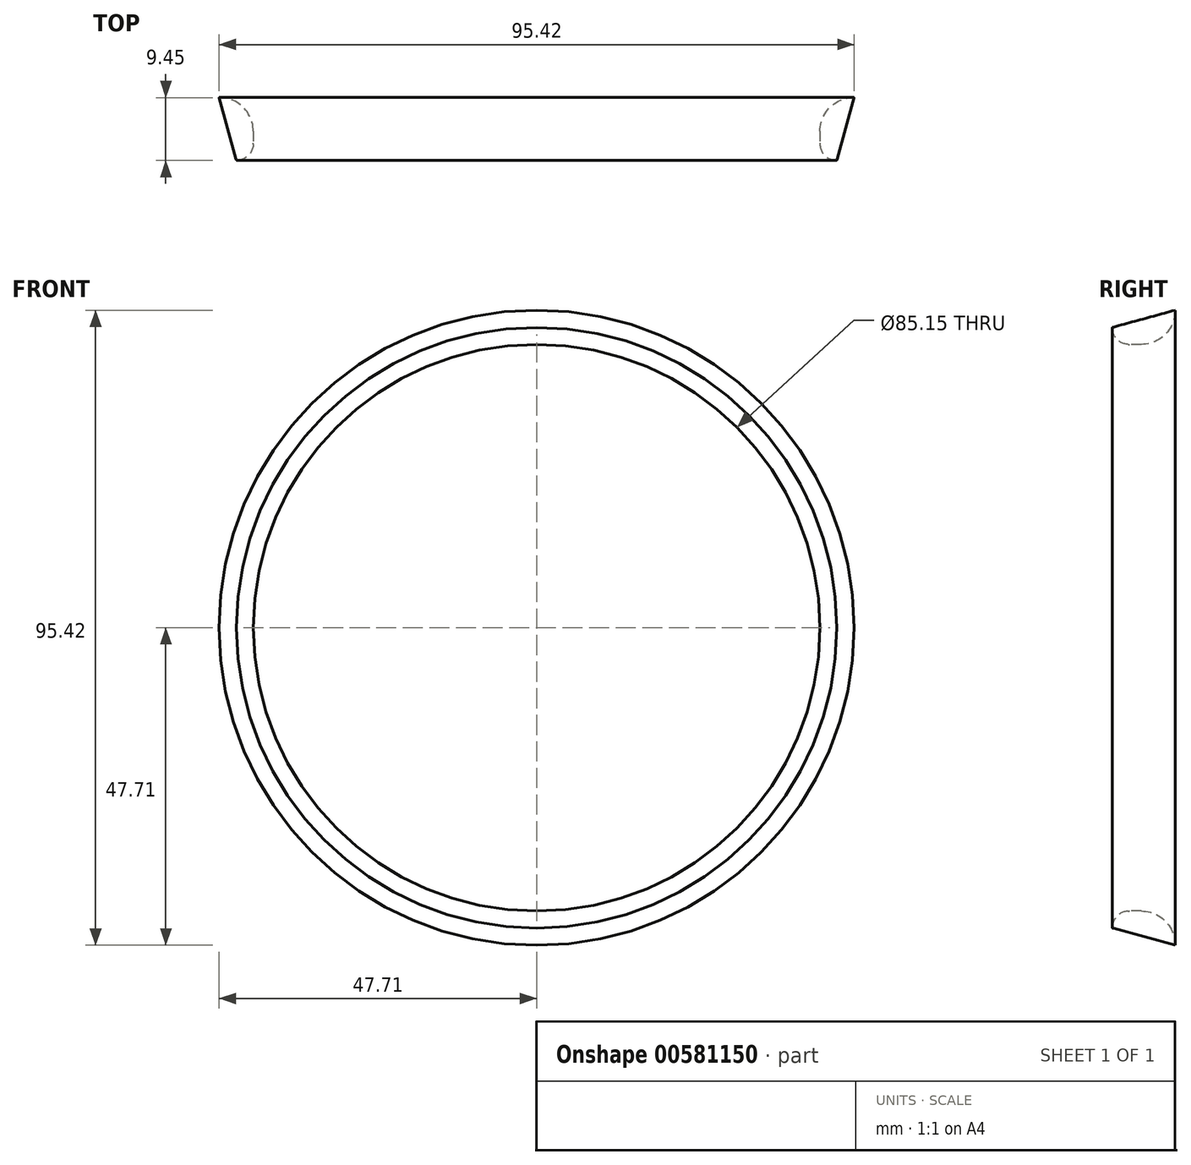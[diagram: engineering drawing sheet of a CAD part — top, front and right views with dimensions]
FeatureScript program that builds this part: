
annotation { "Feature Type Name" : "Feature", "Feature Type Description" : "" }
export const myFeature = defineFeature(function(context is Context, id is Id, definition is map)
    precondition{}
    {
        {
            var Q0;
            Q0=qCreatedBy(makeId("Top.planeOp"),FACE);
            var sketch = newSketch(context, id + "F0", { "sketchPlane" : qUnion([Q0])});
            skArc(sketch, "E0", {"start": v(0, 0) * mm, "mid": v(-32.41, -4.32) * mm, "end": v(-60.63, -20.85) * mm});
            skLineSegment(sketch, "E1", {"start": v(-60.63, -20.85) * mm, "end": v(-43.3, -20.85) * mm});
            skArc(sketch, "E2", {"start": v(0, -9.69) * mm, "mid": v(-22.54, -11.84) * mm, "end": v(-43.3, -20.85) * mm});
            skLineSegment(sketch, "E3", {"start": v(0, 0) * mm, "end": v(0, -9.69) * mm});
            skSolve(sketch);
        }
        {
            var Q0;
            Q0 = qSketchRegion(id + "F0", true);
            var Q1;
            Q1=sQuery(id+"F0.wireOp",EDGE,"E3");
            revolve(context, id + "F1", {"entities" : qUnion([Q0]), "axis" : qUnion([Q1]), "revolveType" : RevolveType.FULL});
        }
        {
            var Q0;
            Q0=qCreatedBy(makeId("Front.planeOp"),FACE);
            var sketch = newSketch(context, id + "F2", { "sketchPlane" : qUnion([Q0])});
            skCircle(sketch, "E4", {"center": v(0, 0) * mm, "radius": 17.75 * mm});
            skSolve(sketch);
        }
        {
            var Q0;
            Q0 = qSketchRegion(id + "F2", true);
            extrude(context, id + "F3", {"entities" : qUnion([Q0]), "operationType" : NewBodyOperationType.REMOVE, "endBound" : BoundingType.SYMMETRIC, "depth" : 25.4 * mm, "offsetDistance" : 25.4 * mm});
        }
        {
            var Q0;
            Q0=qCreatedBy(makeId("Front.planeOp"),FACE);
            var sketch = newSketch(context, id + "F4", { "sketchPlane" : qUnion([Q0])});
            skCircle(sketch, "E5", {"center": v(0, 0) * mm, "radius": 42.57 * mm});
            skSolve(sketch);
        }
        {
            var Q0;
            Q0 = qSketchRegion(id + "F4", true);
            extrude(context, id + "F5", {"entities" : qUnion([Q0]), "operationType" : NewBodyOperationType.REMOVE, "endBound" : BoundingType.SYMMETRIC, "oppositeDirection" : true, "depth" : 114.8 * mm, "offsetDistance" : 25.4 * mm});
        }
        {
            var Q0;
            Q0=makeQuery(id+"F1.opRevolve","SWEPT_EDGE",EDGE,{"disambiguationData":[OSD([sQuery(id+"F0.wireOp",EDGE,"E0"),sQuery(id+"F0.wireOp",EDGE,"E1")])]});
            chamfer(context, id + "F6", {"entities" : qUnion([Q0]), "width" : 5.08 * mm, "tangentPropagation" : true});
        }
        {
            var Q0;
            Q0=makeQuery(id+"F5.boolean.opBoolean","INTERSECT",EDGE,{"derivedFrom":[makeQuery(id+"F1.opRevolve","SWEPT_FACE",FACE,{"disambiguationData":[OSD([sQuery(id+"F0.wireOp",EDGE,"E0")])]}),makeQuery(id+"F5.opExtrude","SWEPT_FACE",FACE,{"disambiguationData":[OSD([sQuery(id+"F4.wireOp",EDGE,"E5")])]})]});
            var Q1;
            Q1=makeQuery(id+"F5.boolean.opBoolean","INTERSECT",EDGE,{"derivedFrom":[makeQuery(id+"F1.opRevolve","SWEPT_FACE",FACE,{"disambiguationData":[OSD([sQuery(id+"F0.wireOp",EDGE,"E2")])]}),makeQuery(id+"F5.opExtrude","SWEPT_FACE",FACE,{"disambiguationData":[OSD([sQuery(id+"F4.wireOp",EDGE,"E5")])]})]});
            fillet(context, id + "F7", {"entities" : qUnion([Q0, Q1]), "radius" : 5.08 * mm, "tangentPropagation" : true, "allowEdgeOverflow" : false});
        }
        {
            var Q0;
            Q0=makeQuery(id+"F7.opFillet","BLEND_EDGE",EDGE,{"blendedFrom":[makeQuery(id+"F5.boolean.opBoolean","INTERSECT",EDGE,{"derivedFrom":[makeQuery(id+"F1.opRevolve","SWEPT_FACE",FACE,{"disambiguationData":[OSD([sQuery(id+"F0.wireOp",EDGE,"E2")])]}),makeQuery(id+"F5.opExtrude","SWEPT_FACE",FACE,{"disambiguationData":[OSD([sQuery(id+"F4.wireOp",EDGE,"E5")])]})]}),makeQuery(id+"F1.opRevolve","SWEPT_FACE",FACE,{"disambiguationData":[OSD([sQuery(id+"F0.wireOp",EDGE,"E1")])]})],"blendedInto":[makeQuery(id+"F1.opRevolve","SWEPT_FACE",FACE,{"disambiguationData":[OSD([sQuery(id+"F0.wireOp",EDGE,"E1")])]})]});
            fillet(context, id + "F8", {"entities" : qUnion([Q0]), "radius" : 2.54 * mm, "tangentPropagation" : true, "allowEdgeOverflow" : false});
        }
        {
            var Q0;
            {var subQ0=sQuery(id+"F0.wireOp",EDGE,"E0");Q0=makeQuery(id+"F6.opChamfer","BLEND_EDGE",EDGE,{"blendedFrom":[makeQuery(id+"F1.opRevolve","SWEPT_EDGE",EDGE,{"disambiguationData":[OSD([subQ0,sQuery(id+"F0.wireOp",EDGE,"E1")])]}),makeQuery(id+"F1.opRevolve","SWEPT_FACE",FACE,{"disambiguationData":[OSD([subQ0])]})],"blendedInto":[makeQuery(id+"F1.opRevolve","SWEPT_FACE",FACE,{"disambiguationData":[OSD([subQ0])]})]});}
            var Q1;
            {var subQ0=sQuery(id+"F0.wireOp",EDGE,"E1");Q1=makeQuery(id+"F6.opChamfer","BLEND_EDGE",EDGE,{"blendedFrom":[makeQuery(id+"F1.opRevolve","SWEPT_EDGE",EDGE,{"disambiguationData":[OSD([sQuery(id+"F0.wireOp",EDGE,"E0"),subQ0])]}),makeQuery(id+"F1.opRevolve","SWEPT_FACE",FACE,{"disambiguationData":[OSD([subQ0])]})],"blendedInto":[makeQuery(id+"F1.opRevolve","SWEPT_FACE",FACE,{"disambiguationData":[OSD([subQ0])]})]});}
            fillet(context, id + "F9", {"entities" : qUnion([Q0, Q1]), "radius" : 2.54 * mm, "tangentPropagation" : true, "allowEdgeOverflow" : false});
        }
    });
